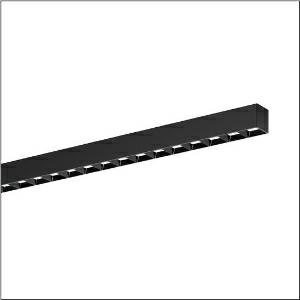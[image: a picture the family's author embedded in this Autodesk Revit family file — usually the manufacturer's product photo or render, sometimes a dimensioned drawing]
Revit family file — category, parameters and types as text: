
# Revit family: silica_r__21_51mx22dc4abb_087a
name_source: partatom
category: Lighting Fixtures
units: mm (PartAtom-declared; Revit-internal decimal feet)

## family parameters
Cut with Voids When Loaded = No
Host = Face
Light Source = No
Part Type = Normal
Room Calculation Point = No
Round Connector Dimension = Use Diameter
Shared = No

## types (1)
- --- (1 x LED, 10800 lm, 64.7 W, 4000K)
    Apparent Load = 65 VA
    CIE Flux Codes = 86 100 100 100 100
    Color Rendering = 80
    Color Temperature = 4000K
    Default Elevation = 1800 mm
    Description = Silica® 21, office luminaire, primary light control with darklight reflector, of PMMA, black, CAT 2 (L<= 3000cd/m²), light emission: direct distribution, primary light characteristic: symmetric, installation type: surface-mounted, LED, rated luminous flux: 10.800lm, luminous efficacy: 167lm/W, light colour: 840, colour temperature: 4000K, control gear: DALI 2, with terminal, 3+2-pole, max. 2.5mm², mains connection: 220..240V, AC, 50/60Hz, rated input power: 64.7W, luminaire housing, of aluminium, matt jet black (RAL 9005), length: 3.004mm, width: 53mm, height: 53mm, protection rating (complete): IP20, insulation class (complete): insulation class I (protective earthing), certification: CE, permissible operating ambient temperature: 0..+35°C, standard: EN 50419, packaging unit: 1 piece
    Height = 53 mm
    Lamp = 1 x LED
    Lamp Light Flux = 10800 lm
    Lamp Power = 64.7 W
    Lamp count = 1
    Length = 3004 mm
    Luminous efficacy = 167 lm/W
    Manufacturer = Siteco
    ModVariant = No
    Model = 51MX22DC4ABB
    Mounting Place = Ceiling
    Mounting Type = Surface mounted
    Number of Poles = 1
    OnlyDefault = Yes
    Power Factor = 1
    Product Name = Silica® 21
    Product group = office luminaire | ceiling mounted
    ProductGroupID = 302
    Protection Class = Protection class I
    Protection Degree = IP 20
    RLX_Detail_Level = 1
    RLX_Emergency_Light_Flux = 0 lm
    RLX_Emergency_Type = 0
    RLX_Emergency_Type_DB = No
    RlxData = <blob elided: 63905 chars, md5=d45b845c>
    Socket = socket
    Standby Power = 0 W
    System Light Flux = 10800 lm
    System Power = 65 W
    Type Comments = factory setting: luminous flux: 100 % | dim-lin: 254 | 366 mA
    Type Image = l_1335908.jpg
    URL = http://relux.com
    VarID = @adj_124714
    Voltage = 0 V
    Weight = 0.00 kg
    Width = 53 mm

## geometry (parser evidence)
native form markers: Blend x4, Sweep x10
no freeform markers — native parametric forms only
